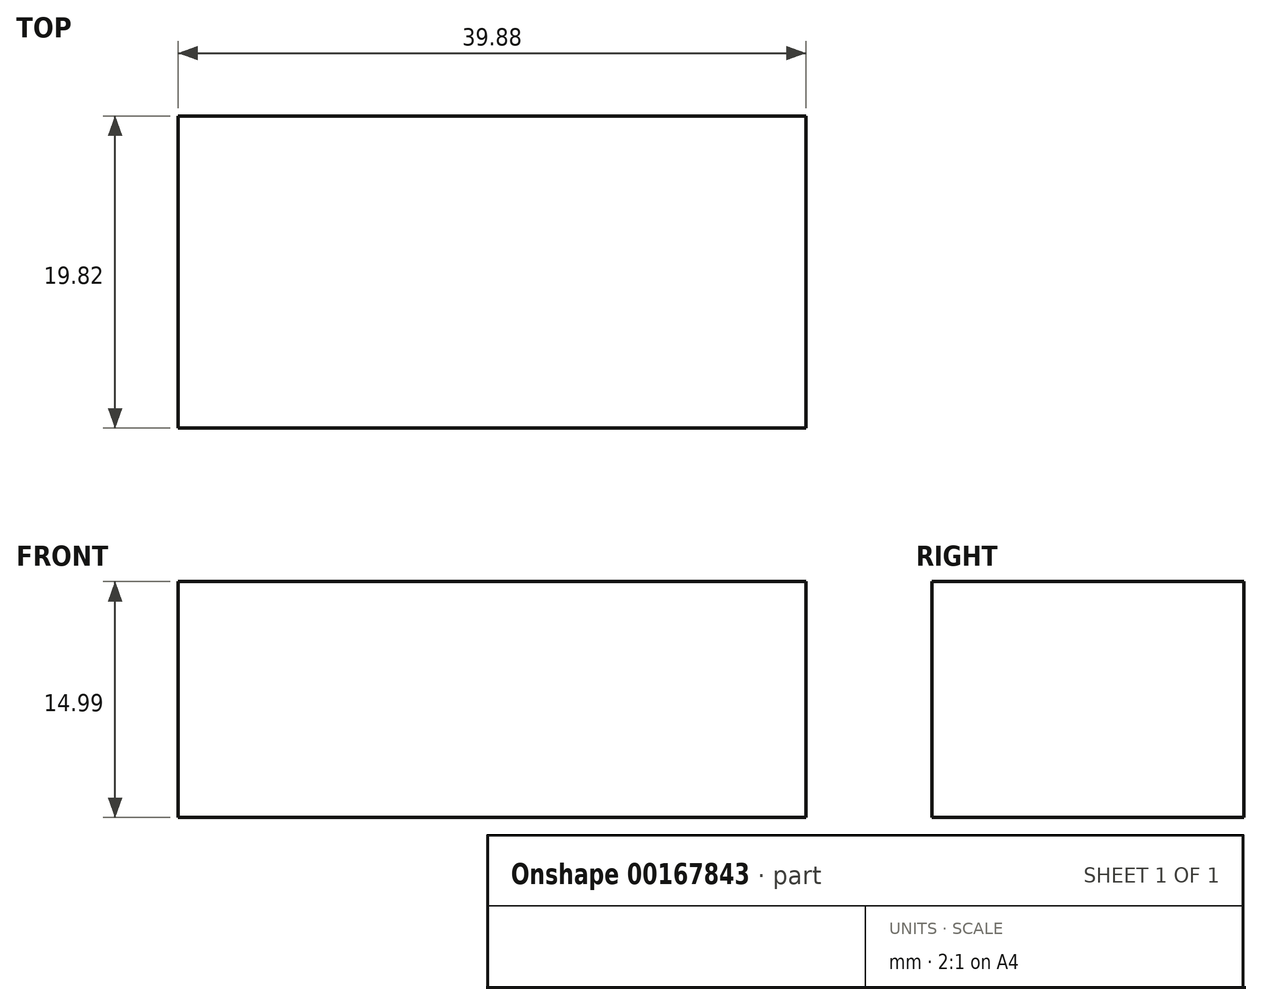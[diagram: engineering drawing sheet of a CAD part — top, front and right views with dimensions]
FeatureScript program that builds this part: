
annotation { "Feature Type Name" : "Feature", "Feature Type Description" : "" }
export const myFeature = defineFeature(function(context is Context, id is Id, definition is map)
    precondition{}
    {
        {
            var Q0;
            Q0=qCreatedBy(makeId("Top.planeOp"),FACE);
            var sketch = newSketch(context, id + "F0", { "sketchPlane" : qUnion([Q0])});
            skLineSegment(sketch, "E0.bottom", {"start": v(19.94, 9.9) * mm, "end": v(-19.94, 9.9) * mm});
            skLineSegment(sketch, "E0.top", {"start": v(19.94, -9.9) * mm, "end": v(-19.94, -9.9) * mm});
            skLineSegment(sketch, "E0.left", {"start": v(19.94, 9.9) * mm, "end": v(19.94, -9.9) * mm});
            skLineSegment(sketch, "E0.right", {"start": v(-19.94, 9.9) * mm, "end": v(-19.94, -9.9) * mm});
            skPoint(sketch, "E0.middle", {"position": v(0, 0) * mm});
            skSolve(sketch);
        }
        {
            var Q0;
            Q0 = qSketchRegion(id + "F0", true);
            extrude(context, id + "F1", {"entities" : qUnion([Q0]), "depth" : 15 * mm});
        }
    });
